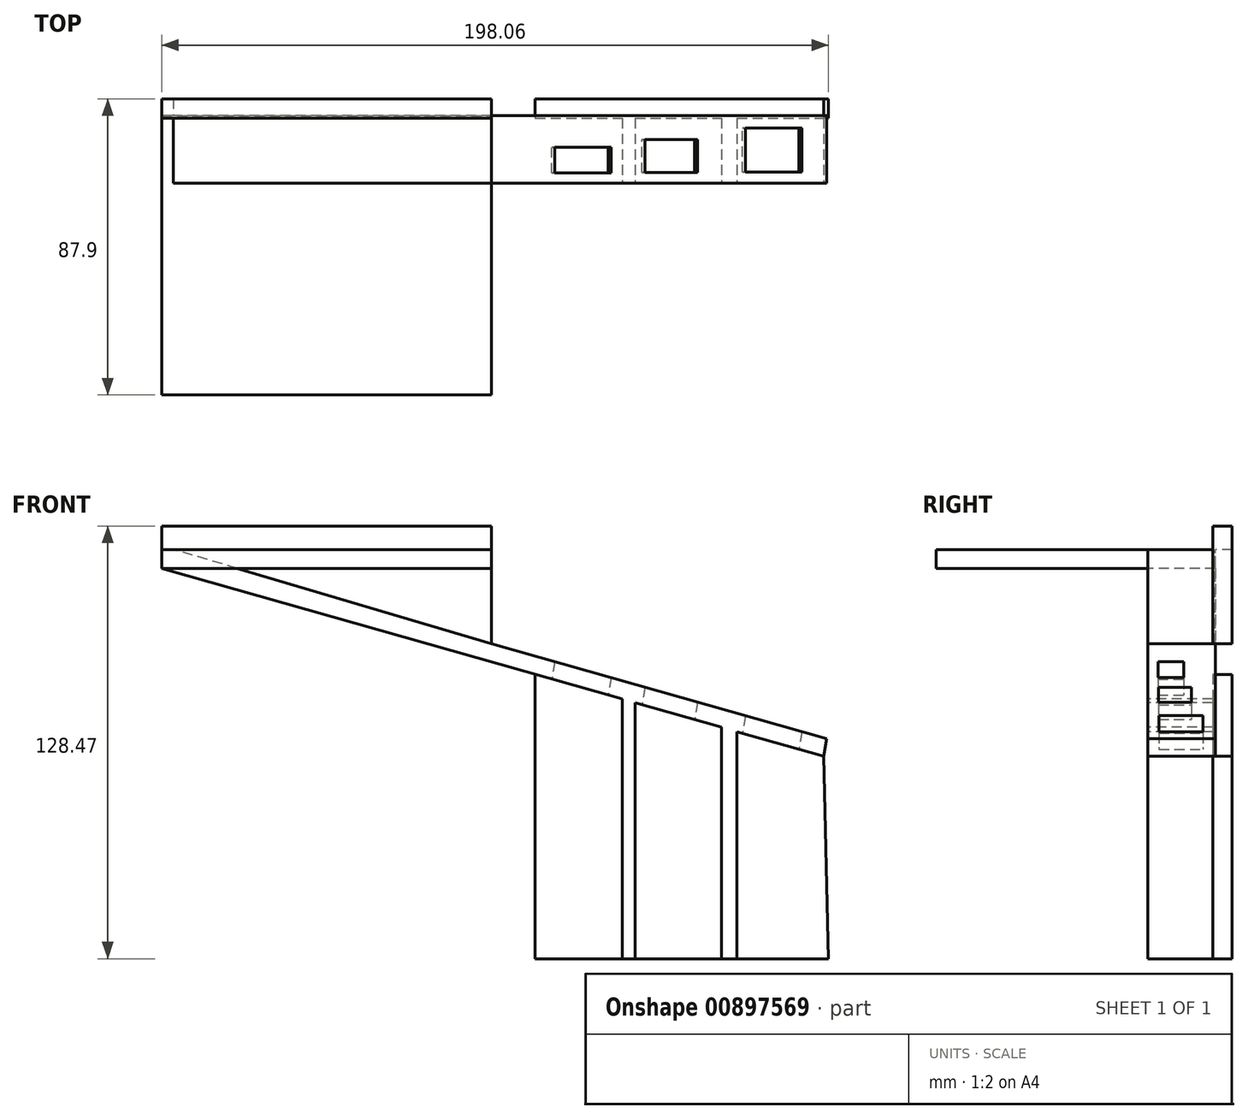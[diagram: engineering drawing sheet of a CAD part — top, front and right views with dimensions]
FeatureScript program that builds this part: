
annotation { "Feature Type Name" : "Feature", "Feature Type Description" : "" }
export const myFeature = defineFeature(function(context is Context, id is Id, definition is map)
    precondition{}
    {
        {
            var Q0;
            Q0=qCreatedBy(makeId("Front.planeOp"),FACE);
            var sketch = newSketch(context, id + "F0", { "sketchPlane" : qUnion([Q0])});
            skLineSegment(sketch, "E0.bottom", {"start": v(0, 0) * mm, "end": v(-98.02, 0) * mm});
            skLineSegment(sketch, "E0.top", {"start": v(0, 5.6) * mm, "end": v(-98.02, 5.6) * mm});
            skLineSegment(sketch, "E0.left", {"start": v(0, 0) * mm, "end": v(0, 5.6) * mm});
            skLineSegment(sketch, "E0.right", {"start": v(-98.02, 0) * mm, "end": v(-98.02, 5.6) * mm});
            skLineSegment(sketch, "E1", {"start": v(-98.02, 0) * mm, "end": v(98.6, -55.8) * mm});
            skLineSegment(sketch, "E2", {"start": v(-98.02, 5.6) * mm, "end": v(-98.02, 12.54) * mm});
            skLineSegment(sketch, "E3", {"start": v(-98.02, 12.54) * mm, "end": v(0, 12.54) * mm});
            skLineSegment(sketch, "E4", {"start": v(0, 12.54) * mm, "end": v(0, 5.6) * mm});
            skLineSegment(sketch, "E5", {"start": v(0, 0) * mm, "end": v(0, -22.36) * mm});
            skLineSegment(sketch, "E6", {"start": v(0, -22.36) * mm, "end": v(99.54, -50.6) * mm});
            skLineSegment(sketch, "E7", {"start": v(99.54, -50.6) * mm, "end": v(98.6, -55.8) * mm});
            skLineSegment(sketch, "E8", {"start": v(0, -22.36) * mm, "end": v(-94.5, 5.6) * mm});
            skLineSegment(sketch, "E9", {"start": v(12.95, -31.49) * mm, "end": v(12.95, -115.93) * mm});
            skLineSegment(sketch, "E10", {"start": v(12.95, -115.93) * mm, "end": v(100.04, -115.93) * mm});
            skLineSegment(sketch, "E11", {"start": v(100.04, -115.93) * mm, "end": v(98.6, -55.8) * mm});
            skLineSegment(sketch, "E12", {"start": v(38.78, -115.93) * mm, "end": v(38.78, -38.82) * mm});
            skLineSegment(sketch, "E13", {"start": v(42.6, -115.93) * mm, "end": v(42.6, -39.9) * mm});
            skLineSegment(sketch, "E14", {"start": v(68.3, -115.93) * mm, "end": v(68.3, -47.2) * mm});
            skLineSegment(sketch, "E15", {"start": v(72.89, -115.93) * mm, "end": v(72.89, -48.5) * mm});
            skSolve(sketch);
        }
        {
            var Q0;
            {var subQ0=sQuery(id+"F0.wireOp",EDGE,"E0.left");Q0=makeQuery(id+"F0.imprint","IMPRINT",FACE,{"disambiguationData":[TD([[makeQuery(id+"F0.imprint","IMPRINT",EDGE,{"derivedFrom":subQ0}),1.0]])]});}
            var Q1;
            {var subQ0=sQuery(id+"F0.wireOp",EDGE,"E0.right");Q1=makeQuery(id+"F0.imprint","IMPRINT",FACE,{"disambiguationData":[TD([[makeQuery(id+"F0.imprint","IMPRINT",EDGE,{"derivedFrom":subQ0}),-1.0]])]});}
            extrude(context, id + "F1", {"entities" : qUnion([Q0, Q1]), "depth" : 62.9 * mm, "offsetDistance" : 25 * mm});
        }
        {
            var Q0;
            {var subQ0=sQuery(id+"F0.wireOp",EDGE,"E1");Q0=makeQuery(id+"F0.imprint","IMPRINT",FACE,{"disambiguationData":[TD([[makeQuery(id+"F0.imprint","IMPRINT",EDGE,{"derivedFrom":subQ0}),1.0]])]});}
            var Q1;
            {var subQ0=sQuery(id+"F0.wireOp",EDGE,"E0.right");Q1=makeQuery(id+"F0.imprint","IMPRINT",FACE,{"disambiguationData":[TD([[makeQuery(id+"F0.imprint","IMPRINT",EDGE,{"derivedFrom":subQ0}),-1.0]])]});}
            var Q2;
            {var subQ0=sQuery(id+"F0.wireOp",EDGE,"E14");Q2=makeQuery(id+"F0.imprint","IMPRINT",FACE,{"disambiguationData":[TD([[makeQuery(id+"F0.imprint","IMPRINT",EDGE,{"derivedFrom":subQ0}),-1.0]])]});}
            var Q3;
            {var subQ0=sQuery(id+"F0.wireOp",EDGE,"E12");Q3=makeQuery(id+"F0.imprint","IMPRINT",FACE,{"disambiguationData":[TD([[makeQuery(id+"F0.imprint","IMPRINT",EDGE,{"derivedFrom":subQ0}),-1.0]])]});}
            extrude(context, id + "F2", {"entities" : qUnion([Q0, Q1, Q2, Q3]), "operationType" : NewBodyOperationType.ADD, "oppositeDirection" : true, "depth" : 20 * mm, "offsetDistance" : 25 * mm});
        }
        {
            var Q0;
            {var subQ0=sQuery(id+"F0.wireOp",EDGE,"E5");Q0=makeQuery(id+"F0.imprint","IMPRINT",FACE,{"disambiguationData":[TD([[makeQuery(id+"F0.imprint","IMPRINT",EDGE,{"derivedFrom":subQ0}),-1.0]])]});}
            var Q1;
            {var subQ0=sQuery(id+"F0.wireOp",EDGE,"E0.left");Q1=makeQuery(id+"F0.imprint","IMPRINT",FACE,{"disambiguationData":[TD([[makeQuery(id+"F0.imprint","IMPRINT",EDGE,{"derivedFrom":subQ0}),1.0]])]});}
            var Q2;
            {var subQ0=sQuery(id+"F0.wireOp",EDGE,"E2");Q2=makeQuery(id+"F0.imprint","IMPRINT",FACE,{"disambiguationData":[TD([[makeQuery(id+"F0.imprint","IMPRINT",EDGE,{"derivedFrom":subQ0}),-1.0]])]});}
            var Q3;
            {var subQ0=sQuery(id+"F0.wireOp",EDGE,"E9");Q3=makeQuery(id+"F0.imprint","IMPRINT",FACE,{"disambiguationData":[TD([[makeQuery(id+"F0.imprint","IMPRINT",EDGE,{"derivedFrom":subQ0}),1.0]])]});}
            var Q4;
            {var subQ0=sQuery(id+"F0.wireOp",EDGE,"E13");Q4=makeQuery(id+"F0.imprint","IMPRINT",FACE,{"disambiguationData":[TD([[makeQuery(id+"F0.imprint","IMPRINT",EDGE,{"derivedFrom":subQ0}),-1.0]])]});}
            var Q5;
            {var subQ0=sQuery(id+"F0.wireOp",EDGE,"E11");Q5=makeQuery(id+"F0.imprint","IMPRINT",FACE,{"disambiguationData":[TD([[makeQuery(id+"F0.imprint","IMPRINT",EDGE,{"derivedFrom":subQ0}),1.0]])]});}
            var Q6;
            {var subQ0=sQuery(id+"F0.wireOp",EDGE,"E12");Q6=makeQuery(id+"F0.imprint","IMPRINT",FACE,{"disambiguationData":[TD([[makeQuery(id+"F0.imprint","IMPRINT",EDGE,{"derivedFrom":subQ0}),-1.0]])]});}
            var Q7;
            {var subQ0=sQuery(id+"F0.wireOp",EDGE,"E14");Q7=makeQuery(id+"F0.imprint","IMPRINT",FACE,{"disambiguationData":[TD([[makeQuery(id+"F0.imprint","IMPRINT",EDGE,{"derivedFrom":subQ0}),-1.0]])]});}
            extrude(context, id + "F3", {"entities" : qUnion([Q0, Q1, Q2, Q3, Q4, Q5, Q6, Q7]), "operationType" : NewBodyOperationType.ADD, "oppositeDirection" : true, "depth" : 25 * mm, "offsetDistance" : 25 * mm, "hasSecondDirection" : true, "secondDirectionOppositeDirection" : true, "secondDirectionDepth" : 19.2 * mm});
        }
        {
            var Q0;
            Q0=makeQuery(id+"F2.opExtrude","SWEPT_FACE",FACE,{"disambiguationData":[OSD([sQuery(id+"F0.wireOp",EDGE,"E6")])]});
            var sketch = newSketch(context, id + "F4", { "sketchPlane" : qUnion([Q0])});
            skLineSegment(sketch, "E16.bottom", {"start": v(25.64, 2.96) * mm, "end": v(43.04, 2.96) * mm});
            skLineSegment(sketch, "E16.top", {"start": v(25.64, 10.68) * mm, "end": v(43.04, 10.68) * mm});
            skLineSegment(sketch, "E16.left", {"start": v(25.64, 2.96) * mm, "end": v(25.64, 10.68) * mm});
            skLineSegment(sketch, "E16.right", {"start": v(43.04, 2.96) * mm, "end": v(43.04, 10.68) * mm});
            skLineSegment(sketch, "E17.bottom", {"start": v(53.48, 3.11) * mm, "end": v(69.68, 3.11) * mm});
            skLineSegment(sketch, "E17.top", {"start": v(53.48, 12.95) * mm, "end": v(69.68, 12.95) * mm});
            skLineSegment(sketch, "E17.left", {"start": v(53.48, 3.11) * mm, "end": v(53.48, 12.95) * mm});
            skLineSegment(sketch, "E17.right", {"start": v(69.68, 3.11) * mm, "end": v(69.68, 12.95) * mm});
            skLineSegment(sketch, "E18.bottom", {"start": v(84.5, 3.29) * mm, "end": v(101.95, 3.29) * mm});
            skLineSegment(sketch, "E18.top", {"start": v(84.5, 16.28) * mm, "end": v(101.95, 16.28) * mm});
            skLineSegment(sketch, "E18.left", {"start": v(84.5, 3.29) * mm, "end": v(84.5, 16.28) * mm});
            skLineSegment(sketch, "E18.right", {"start": v(101.95, 3.29) * mm, "end": v(101.95, 16.28) * mm});
            skSolve(sketch);
        }
        {
            var Q0;
            Q0=makeQuery(id+"F4.imprint","IMPRINT",FACE,{"disambiguationData":[TD([[makeQuery(id+"F4.imprint","IMPRINT",EDGE,{"derivedFrom":sQuery(id+"F4.wireOp",EDGE,"E16.bottom")}),1.0]])]});
            var Q1;
            Q1=makeQuery(id+"F4.imprint","IMPRINT",FACE,{"disambiguationData":[TD([[makeQuery(id+"F4.imprint","IMPRINT",EDGE,{"derivedFrom":sQuery(id+"F4.wireOp",EDGE,"E17.bottom")}),1.0]])]});
            var Q2;
            Q2=makeQuery(id+"F4.imprint","IMPRINT",FACE,{"disambiguationData":[TD([[makeQuery(id+"F4.imprint","IMPRINT",EDGE,{"derivedFrom":sQuery(id+"F4.wireOp",EDGE,"E18.bottom")}),1.0]])]});
            var Q3;
            Q3=sQuery(id+"F0.wireOp",EDGE,"E7");
            sweep(context, id + "F5", {"operationType" : NewBodyOperationType.REMOVE, "profiles" : qUnion([Q0, Q1, Q2]), "path" : qUnion([Q3])});
        }
    });
